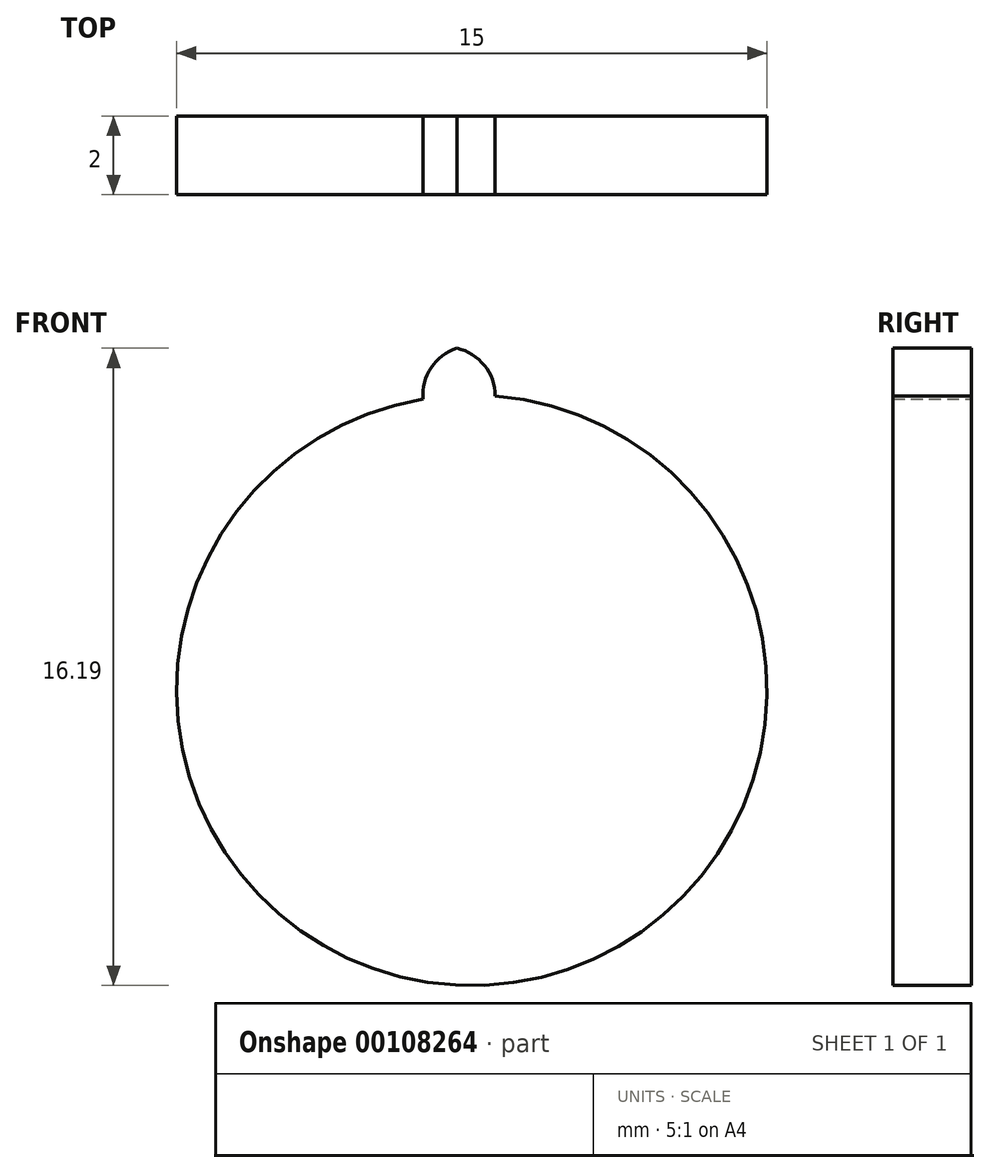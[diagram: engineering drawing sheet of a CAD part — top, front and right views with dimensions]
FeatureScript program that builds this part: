
annotation { "Feature Type Name" : "Feature", "Feature Type Description" : "" }
export const myFeature = defineFeature(function(context is Context, id is Id, definition is map)
    precondition{}
    {
        {
            var Q0;
            Q0=qCreatedBy(makeId("Front.planeOp"),FACE);
            var sketch = newSketch(context, id + "F0", { "sketchPlane" : qUnion([Q0])});
            skCircle(sketch, "E0", {"center": v(0, 0) * mm, "radius": 7.5 * mm});
            skCircle(sketch, "E1", {"center": v(0, 0) * mm, "radius": 8.75 * mm, "construction": true});
            skCircle(sketch, "E2", {"center": v(0, 0) * mm, "radius": 10 * mm, "construction": true});
            skCircle(sketch, "E3", {"center": v(0, 7.5) * mm, "radius": 1.25 * mm, "construction": true});
            skLineSegment(sketch, "E4", {"start": v(0, 0) * mm, "end": v(0, 10.41) * mm, "construction": true});
            skLineSegment(sketch, "E5", {"start": v(0, 0) * mm, "end": v(-0.92, 10.55) * mm, "construction": true});
            skCircle(sketch, "E6", {"center": v(-0.65, 7.47) * mm, "radius": 1.25 * mm, "construction": true});
            skArc(sketch, "E7", {"start": v(-0.38, 8.7) * mm, "mid": v(-1.24, 7.6) * mm, "end": v(-0.56, 6.38) * mm});
            skArc(sketch, "E8", {"start": v(0, 6.4) * mm, "mid": v(0.58, 7.68) * mm, "end": v(-0.38, 8.7) * mm});
            skSolve(sketch);
        }
        {
            var Q0;
            {var subQ0=sQuery(id+"F0.wireOp",EDGE,"E0");var subQ1=makeQuery(id+"F0.imprint","INTERSECT",VERTEX,{"derivedFrom":[subQ0,sQuery(id+"F0.wireOp",EDGE,"E7")]});Q0=makeQuery(id+"F0.imprint","IMPRINT",FACE,{"disambiguationData":[TD([[makeQuery(id+"F0.imprint","IMPRINT",EDGE,{"disambiguationData":[TD([[subQ1,1.0]])],"derivedFrom":subQ0}),1.0]])]});}
            var Q1;
            {var subQ0=sQuery(id+"F0.wireOp",EDGE,"E7");var subQ1=sQuery(id+"F0.wireOp",EDGE,"E0");var subQ2=makeQuery(id+"F0.imprint","INTERSECT",VERTEX,{"derivedFrom":[subQ1,subQ0]});Q1=makeQuery(id+"F0.imprint","IMPRINT",FACE,{"disambiguationData":[TD([[makeQuery(id+"F0.imprint","IMPRINT",EDGE,{"disambiguationData":[TD([[subQ2,1.0]])],"derivedFrom":subQ1}),-1.0]])]});}
            extrude(context, id + "F1", {"entities" : qUnion([Q0, Q1]), "depth" : 2 * mm});
        }
    });
